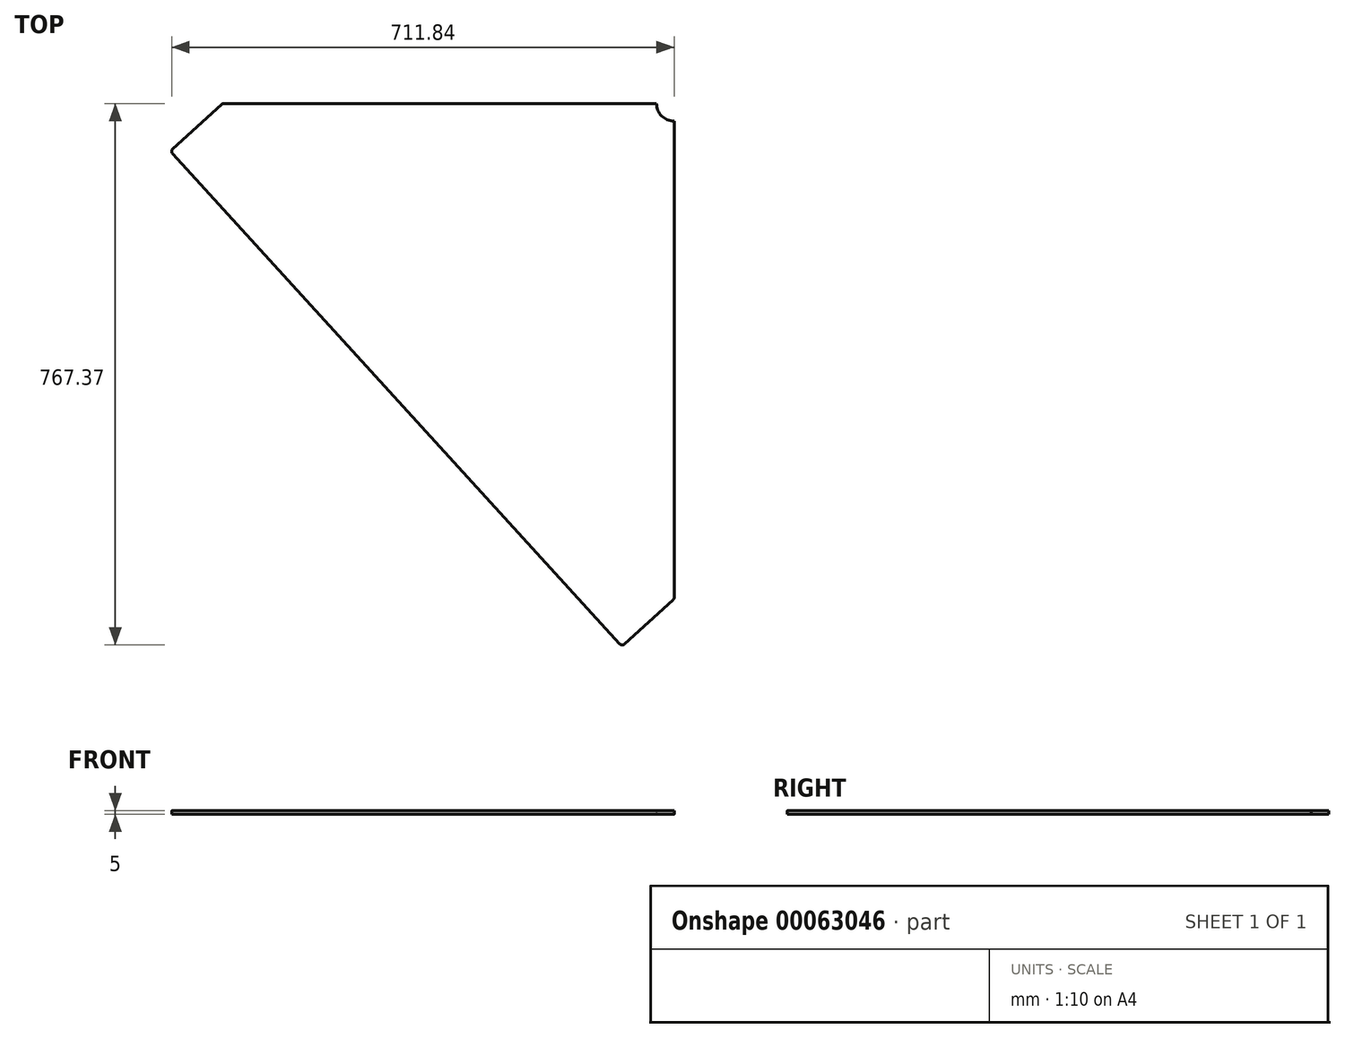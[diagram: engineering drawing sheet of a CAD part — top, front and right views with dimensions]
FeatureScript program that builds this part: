
annotation { "Feature Type Name" : "Feature", "Feature Type Description" : "" }
export const myFeature = defineFeature(function(context is Context, id is Id, definition is map)
    precondition{}
    {
        {
            var Q0;
            Q0=qCreatedBy(makeId("Top.planeOp"),FACE);
            var sketch = newSketch(context, id + "F0", { "sketchPlane" : qUnion([Q0])});
            skLineSegment(sketch, "E0", {"start": v(-25, 0) * mm, "end": v(-638.06, 0) * mm});
            skLineSegment(sketch, "E1", {"start": v(-710.53, -71.06) * mm, "end": v(-77.27, -765.74) * mm});
            skLineSegment(sketch, "E2", {"start": v(-70.2, -766.07) * mm, "end": v(-1.63, -703.56) * mm});
            skLineSegment(sketch, "E3", {"start": v(0, -699.86) * mm, "end": v(0, -25) * mm});
            skLineSegment(sketch, "E4", {"start": v(-710.2, -64) * mm, "end": v(-641.43, -1.3) * mm});
            skArc(sketch, "E5", {"start": v(-25, 0) * mm, "mid": v(-17.68, -17.68) * mm, "end": v(0, -25) * mm});
            skPoint(sketch, "E6.visualSharp", {"position": v(-640, 0) * mm});
            skArc(sketch, "E6.filletArc", {"start": v(-638.06, 0) * mm, "mid": v(-639.87, -0.34) * mm, "end": v(-641.43, -1.3) * mm});
            skPoint(sketch, "E7.visualSharp", {"position": v(-713.9, -67.37) * mm});
            skArc(sketch, "E7.filletArc", {"start": v(-710.2, -64) * mm, "mid": v(-711.83, -67.46) * mm, "end": v(-710.53, -71.06) * mm});
            skPoint(sketch, "E8.visualSharp", {"position": v(-73.9, -769.44) * mm});
            skArc(sketch, "E8.filletArc", {"start": v(-77.27, -765.74) * mm, "mid": v(-73.8, -767.37) * mm, "end": v(-70.2, -766.07) * mm});
            skPoint(sketch, "E9.visualSharp", {"position": v(0, -702.07) * mm});
            skArc(sketch, "E9.filletArc", {"start": v(-1.63, -703.56) * mm, "mid": v(-0.43, -701.88) * mm, "end": v(0, -699.86) * mm});
            skSolve(sketch);
        }
        {
            var Q0;
            Q0=makeQuery(id+"F0.imprint","IMPRINT",FACE,{"disambiguationData":[TD([[makeQuery(id+"F0.imprint","IMPRINT",EDGE,{"derivedFrom":sQuery(id+"F0.wireOp",EDGE,"E0")}),1.0]])]});
            extrude(context, id + "F1", {"entities" : qUnion([Q0]), "depth" : 5 * mm});
        }
    });
